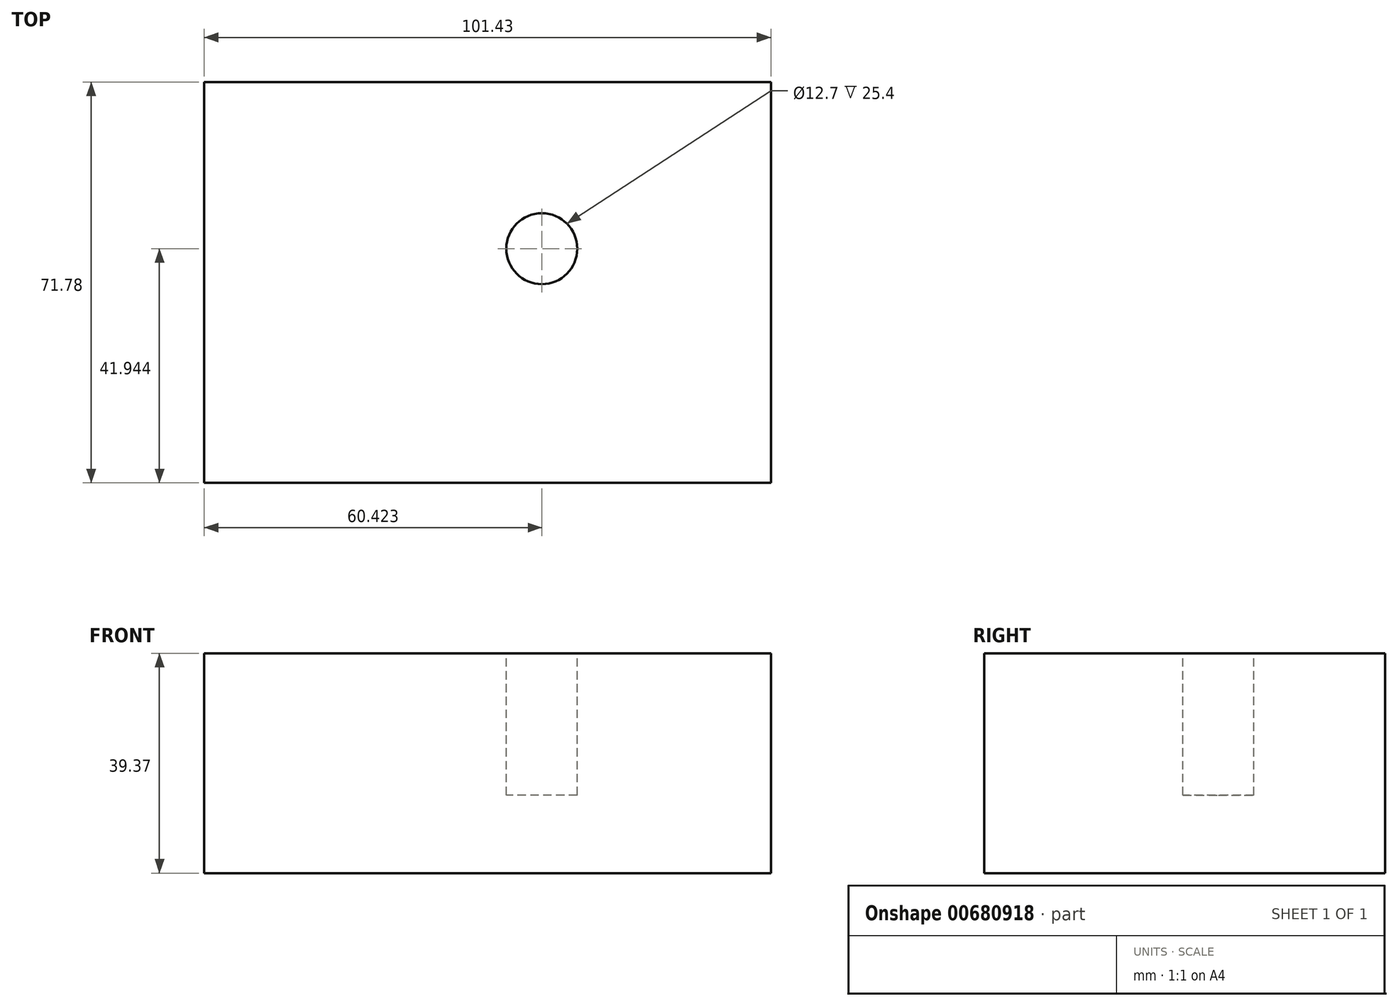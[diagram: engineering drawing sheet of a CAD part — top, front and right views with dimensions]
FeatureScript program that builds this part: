
annotation { "Feature Type Name" : "Feature", "Feature Type Description" : "" }
export const myFeature = defineFeature(function(context is Context, id is Id, definition is map)
    precondition{}
    {
        {
            var Q0;
            Q0=qCreatedBy(makeId("Top.planeOp"),FACE);
            var sketch = newSketch(context, id + "F0", { "sketchPlane" : qUnion([Q0])});
            skLineSegment(sketch, "E0", {"start": v(-53.3, -28.4) * mm, "end": v(48.13, -28.4) * mm});
            skLineSegment(sketch, "E1", {"start": v(48.13, -28.4) * mm, "end": v(48.13, 43.38) * mm});
            skLineSegment(sketch, "E2", {"start": v(48.13, 43.38) * mm, "end": v(-53.3, 43.38) * mm});
            skLineSegment(sketch, "E3", {"start": v(-53.3, 43.38) * mm, "end": v(-53.3, -28.4) * mm});
            skSolve(sketch);
        }
        {
            var Q0;
            Q0 = qSketchRegion(id + "F0", true);
            extrude(context, id + "F1", {"entities" : qUnion([Q0]), "depth" : 39.37 * mm, "offsetDistance" : 25.4 * mm});
        }
        {
            var Q0;
            Q0=makeQuery(id+"F1.opExtrude","CAP_FACE",FACE,{"disambiguationData":[OSD([sQuery(id+"F0.wireOp",EDGE,"E0"),sQuery(id+"F0.wireOp",EDGE,"E1"),sQuery(id+"F0.wireOp",EDGE,"E2"),sQuery(id+"F0.wireOp",EDGE,"E3")])],"isStart":false});
            var sketch = newSketch(context, id + "F2", { "sketchPlane" : qUnion([Q0])});
            skCircle(sketch, "E4", {"center": v(7.12, 13.54) * mm, "radius": 6.35 * mm});
            skSolve(sketch);
        }
        {
            var Q0;
            Q0 = qSketchRegion(id + "F2", true);
            extrude(context, id + "F3", {"entities" : qUnion([Q0]), "operationType" : NewBodyOperationType.REMOVE, "oppositeDirection" : true, "depth" : 25.4 * mm, "offsetDistance" : 25.4 * mm});
        }
    });
